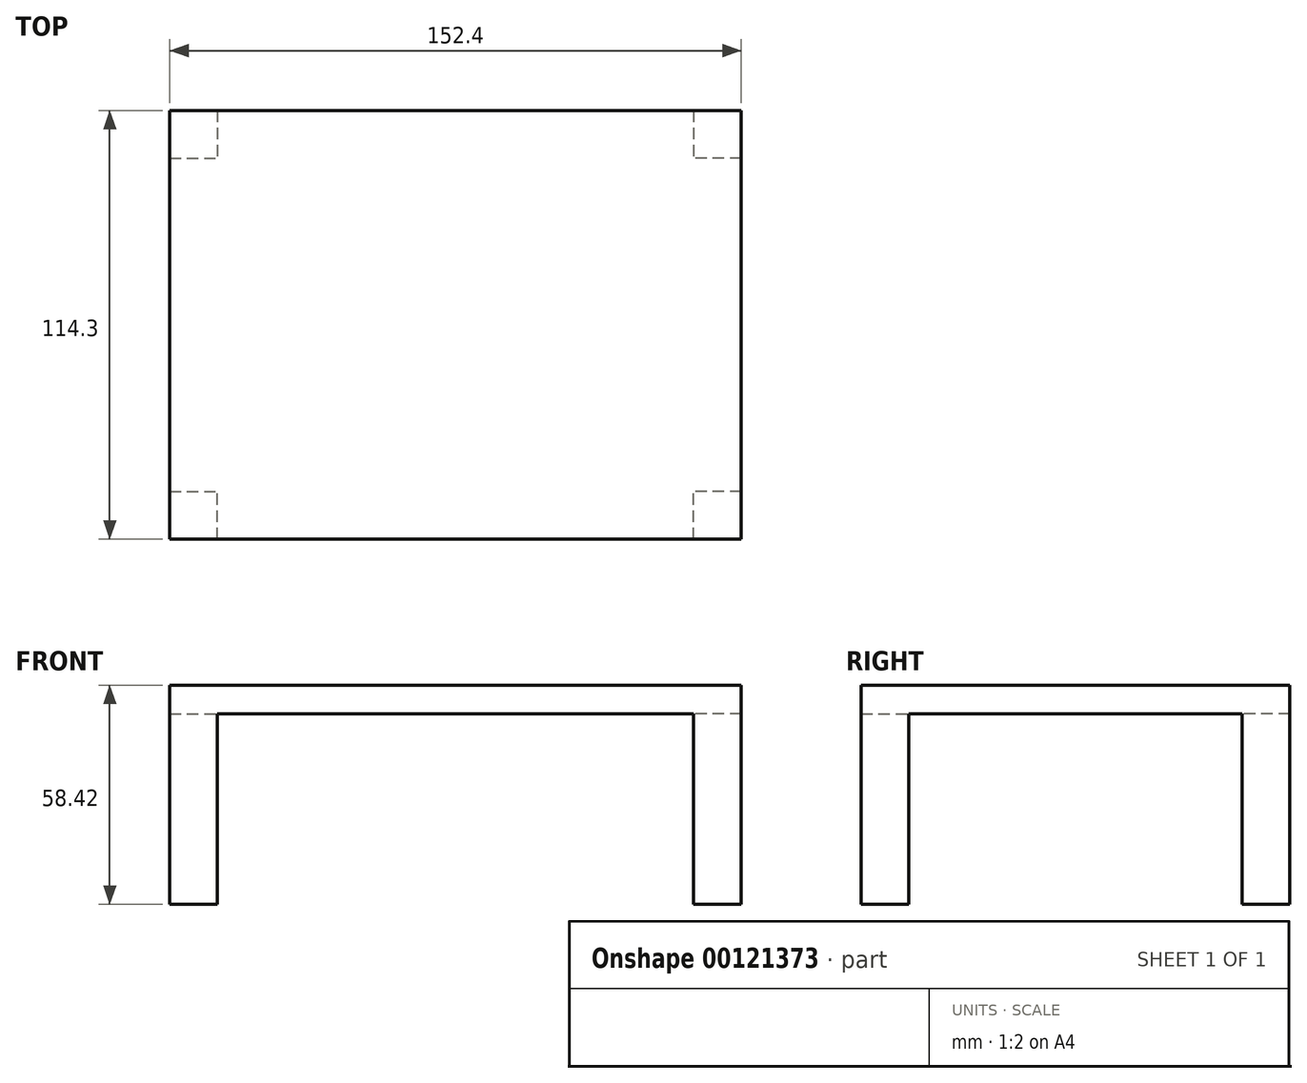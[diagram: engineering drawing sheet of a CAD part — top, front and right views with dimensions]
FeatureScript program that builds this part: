
annotation { "Feature Type Name" : "Feature", "Feature Type Description" : "" }
export const myFeature = defineFeature(function(context is Context, id is Id, definition is map)
    precondition{}
    {
        {
            var Q0;
            Q0=qCreatedBy(makeId("Top.planeOp"),FACE);
            var sketch = newSketch(context, id + "F0", { "sketchPlane" : qUnion([Q0])});
            skLineSegment(sketch, "E0.bottom", {"start": v(76.2, 57.15) * mm, "end": v(-76.2, 57.15) * mm});
            skLineSegment(sketch, "E0.top", {"start": v(76.2, -57.15) * mm, "end": v(-76.2, -57.15) * mm});
            skLineSegment(sketch, "E0.left", {"start": v(76.2, 57.15) * mm, "end": v(76.2, -57.15) * mm});
            skLineSegment(sketch, "E0.right", {"start": v(-76.2, 57.15) * mm, "end": v(-76.2, -57.15) * mm});
            skPoint(sketch, "E0.middle", {"position": v(0, 0) * mm});
            skSolve(sketch);
        }
        {
            var Q0;
            Q0=makeQuery(id+"F0.imprint","IMPRINT",FACE,{"disambiguationData":[TD([[makeQuery(id+"F0.imprint","IMPRINT",EDGE,{"derivedFrom":sQuery(id+"F0.wireOp",EDGE,"E0.bottom")}),1.0]])]});
            extrude(context, id + "F1", {"entities" : qUnion([Q0]), "depth" : 7.62 * mm});
        }
        {
            var Q0;
            Q0=makeQuery(id+"F1.opExtrude","CAP_FACE",FACE,{"disambiguationData":[OSD([sQuery(id+"F0.wireOp",EDGE,"E0.bottom"),sQuery(id+"F0.wireOp",EDGE,"E0.top"),sQuery(id+"F0.wireOp",EDGE,"E0.left"),sQuery(id+"F0.wireOp",EDGE,"E0.right")])],"isStart":true});
            var sketch = newSketch(context, id + "F2", { "sketchPlane" : qUnion([Q0])});
            skLineSegment(sketch, "E1.bottom", {"start": v(-76.2, 57.15) * mm, "end": v(-63.5, 57.15) * mm});
            skLineSegment(sketch, "E1.top", {"start": v(-76.2, 44.45) * mm, "end": v(-63.5, 44.45) * mm});
            skLineSegment(sketch, "E1.left", {"start": v(-76.2, 57.15) * mm, "end": v(-76.2, 44.45) * mm});
            skLineSegment(sketch, "E1.right", {"start": v(-63.5, 57.15) * mm, "end": v(-63.5, 44.45) * mm});
            skLineSegment(sketch, "E2.bottom", {"start": v(76.2, 57.15) * mm, "end": v(63.5, 57.15) * mm});
            skLineSegment(sketch, "E2.top", {"start": v(76.2, 44.45) * mm, "end": v(63.5, 44.45) * mm});
            skLineSegment(sketch, "E2.left", {"start": v(76.2, 57.15) * mm, "end": v(76.2, 44.45) * mm});
            skLineSegment(sketch, "E2.right", {"start": v(63.5, 57.15) * mm, "end": v(63.5, 44.45) * mm});
            skLineSegment(sketch, "E3.bottom", {"start": v(-76.2, -57.15) * mm, "end": v(-63.5, -57.15) * mm});
            skLineSegment(sketch, "E3.top", {"start": v(-76.2, -44.45) * mm, "end": v(-63.5, -44.45) * mm});
            skLineSegment(sketch, "E3.left", {"start": v(-76.2, -57.15) * mm, "end": v(-76.2, -44.45) * mm});
            skLineSegment(sketch, "E3.right", {"start": v(-63.5, -57.15) * mm, "end": v(-63.5, -44.45) * mm});
            skLineSegment(sketch, "E4.bottom", {"start": v(76.2, -57.15) * mm, "end": v(63.5, -57.15) * mm});
            skLineSegment(sketch, "E4.top", {"start": v(76.2, -44.45) * mm, "end": v(63.5, -44.45) * mm});
            skLineSegment(sketch, "E4.left", {"start": v(76.2, -57.15) * mm, "end": v(76.2, -44.45) * mm});
            skLineSegment(sketch, "E4.right", {"start": v(63.5, -57.15) * mm, "end": v(63.5, -44.45) * mm});
            skSolve(sketch);
        }
        {
            var Q0;
            Q0 = qSketchRegion(id + "F2", true);
            extrude(context, id + "F3", {"entities" : qUnion([Q0]), "operationType" : NewBodyOperationType.ADD, "depth" : 50.8 * mm});
        }
    });
